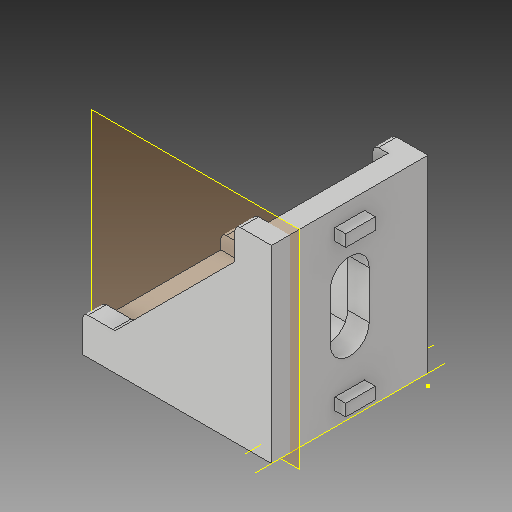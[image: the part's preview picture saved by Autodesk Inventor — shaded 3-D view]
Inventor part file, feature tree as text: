
AUTODESK INVENTOR PART (.ipt)
format: ipt  version: 2018 (Build 220112000, 112)  size: 186,368 bytes
history: native  units: mm
features: sketch x8, other x5, plane x1
ambient origin geometry x8: Origin, YZ Plane, XZ Plane, XY Plane, X Axis, Y Axis, Z Axis, Center Point
bodies: Solid1 (feature_tree)
feature tree (14):
  other  "30mm Bracket_CPY_MIR2_MIR_MIR.ipt"
  other  "Solid1::30mm Bracket_CPY_MIR2_MIR_MIR.ipt"
  other  "TaggingFeature1"
  sketch  "Sketch1"  dims[d0=10.0mm]
  sketch  "Sketch2"
  sketch  "Sketch3"
  sketch  "Sketch4"
  sketch  "Sketch5"
  sketch  "Sketch7"
  sketch  "Sketch9"
  sketch  "Sketch10"
  plane  "Work Plane1"
  other  "Work Axis1"
  other  "Work Axis2"
